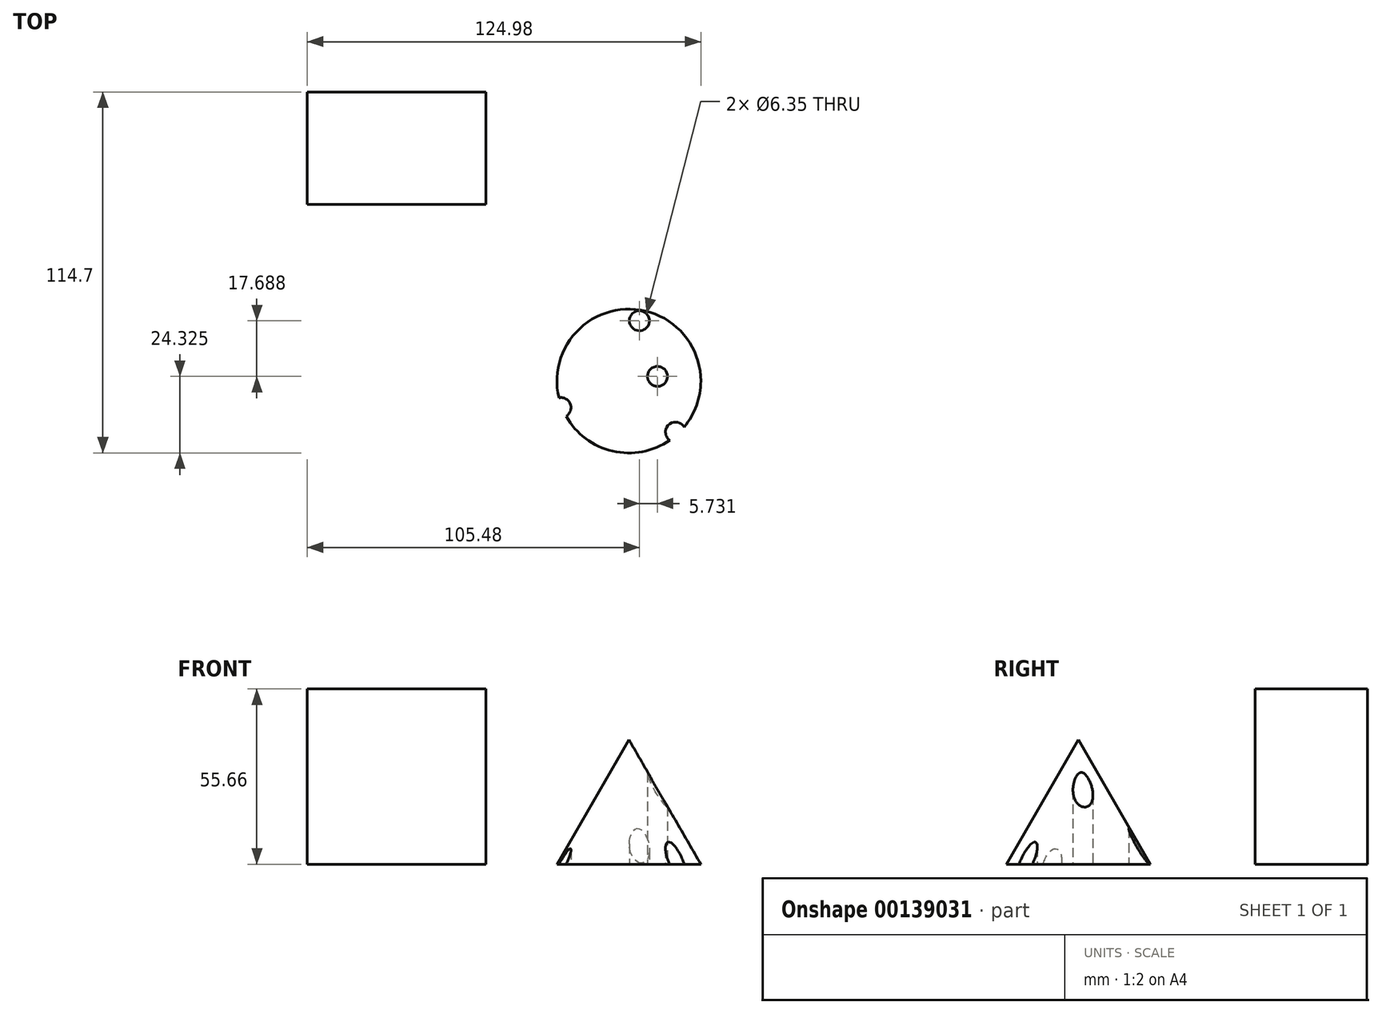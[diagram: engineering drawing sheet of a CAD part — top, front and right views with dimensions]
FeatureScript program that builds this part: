
annotation { "Feature Type Name" : "Feature", "Feature Type Description" : "" }
export const myFeature = defineFeature(function(context is Context, id is Id, definition is map)
    precondition{}
    {
        {
            var Q0;
            Q0=qCreatedBy(makeId("Top.planeOp"),FACE);
            var sketch = newSketch(context, id + "F0", { "sketchPlane" : qUnion([Q0])});
            skLineSegment(sketch, "E0.bottom", {"start": v(-68.5, 48.12) * mm, "end": v(-11.78, 48.12) * mm});
            skLineSegment(sketch, "E0.top", {"start": v(-68.5, 12.42) * mm, "end": v(-11.78, 12.42) * mm});
            skLineSegment(sketch, "E0.left", {"start": v(-68.5, 48.12) * mm, "end": v(-68.5, 12.42) * mm});
            skLineSegment(sketch, "E0.right", {"start": v(-11.78, 48.12) * mm, "end": v(-11.78, 12.42) * mm});
            skSolve(sketch);
        }
        {
            var Q0;
            Q0 = qSketchRegion(id + "F0", true);
            extrude(context, id + "F1", {"entities" : qUnion([Q0]), "depth" : 55.66 * mm});
        }
        {
            var Q0;
            Q0=qCreatedBy(makeId("Top.planeOp"),FACE);
            var sketch = newSketch(context, id + "F2", { "sketchPlane" : qUnion([Q0])});
            skCircle(sketch, "E1", {"center": v(63.19, -4.53) * mm, "radius": 0.93 * mm});
            skCircle(sketch, "E2", {"center": v(33.64, -43.73) * mm, "radius": 22.85 * mm});
            skSolve(sketch);
        }
        {
            var Q0;
            Q0=makeQuery(id+"F2.imprint","IMPRINT",FACE,{"disambiguationData":[TD([[makeQuery(id+"F2.imprint","IMPRINT",EDGE,{"derivedFrom":sQuery(id+"F2.wireOp",EDGE,"E2")}),1.0]])]});
            extrude(context, id + "F3", {"entities" : qUnion([Q0]), "depth" : 44 * mm, "hasDraft" : true, "draftAngle" : 30 * degree, "draftPullDirection" : true});
        }
        {
            var Q0;
            Q0=qCreatedBy(makeId("Top.planeOp"),FACE);
            var sketch = newSketch(context, id + "F4", { "sketchPlane" : qUnion([Q0])});
            skCircle(sketch, "E3.cCircle", {"center": v(32.5, -45.56) * mm, "radius": 10.73 * mm, "construction": true});
            skLineSegment(sketch, "E3.0", {"start": v(37, -24.57) * mm, "end": v(48.45, -59.94) * mm});
            skLineSegment(sketch, "E3.1", {"start": v(48.45, -59.94) * mm, "end": v(12.08, -52.18) * mm});
            skLineSegment(sketch, "E3.2", {"start": v(12.08, -52.18) * mm, "end": v(37, -24.57) * mm});
            skPoint(sketch, "E3.0.midPoint", {"position": v(42.72, -42.25) * mm});
            skSolve(sketch);
        }
        {
            var Q0;
            Q0=sQuery(id+"F4.wireOp",VERTEX,"E3.0.midPoint");
            var Q1;
            Q1=sQuery(id+"F4.wireOp",VERTEX,"E3.2.end");
            var Q2;
            Q2=sQuery(id+"F4.wireOp",VERTEX,"E3.2.start");
            var Q3;
            Q3=sQuery(id+"F4.wireOp",VERTEX,"E3.1.start");
            var Q4;
            Q4=makeQuery(id+"F3.opExtrude","SWEPT_BODY",BODY,{"disambiguationData":[OSD([sQuery(id+"F2.wireOp",EDGE,"E2")])]});
            hole(context, id + "F5", {"style" : HoleStyle.SIMPLE, "endStyle" : HoleEndStyle.THROUGH, "oppositeDirection" : true, "holeDiameter" : 6.35 * mm, "locations" : qUnion([Q0, Q1, Q2, Q3]), "scope" : qUnion([Q4]), "isTappedThrough" : true});
        }
    });
